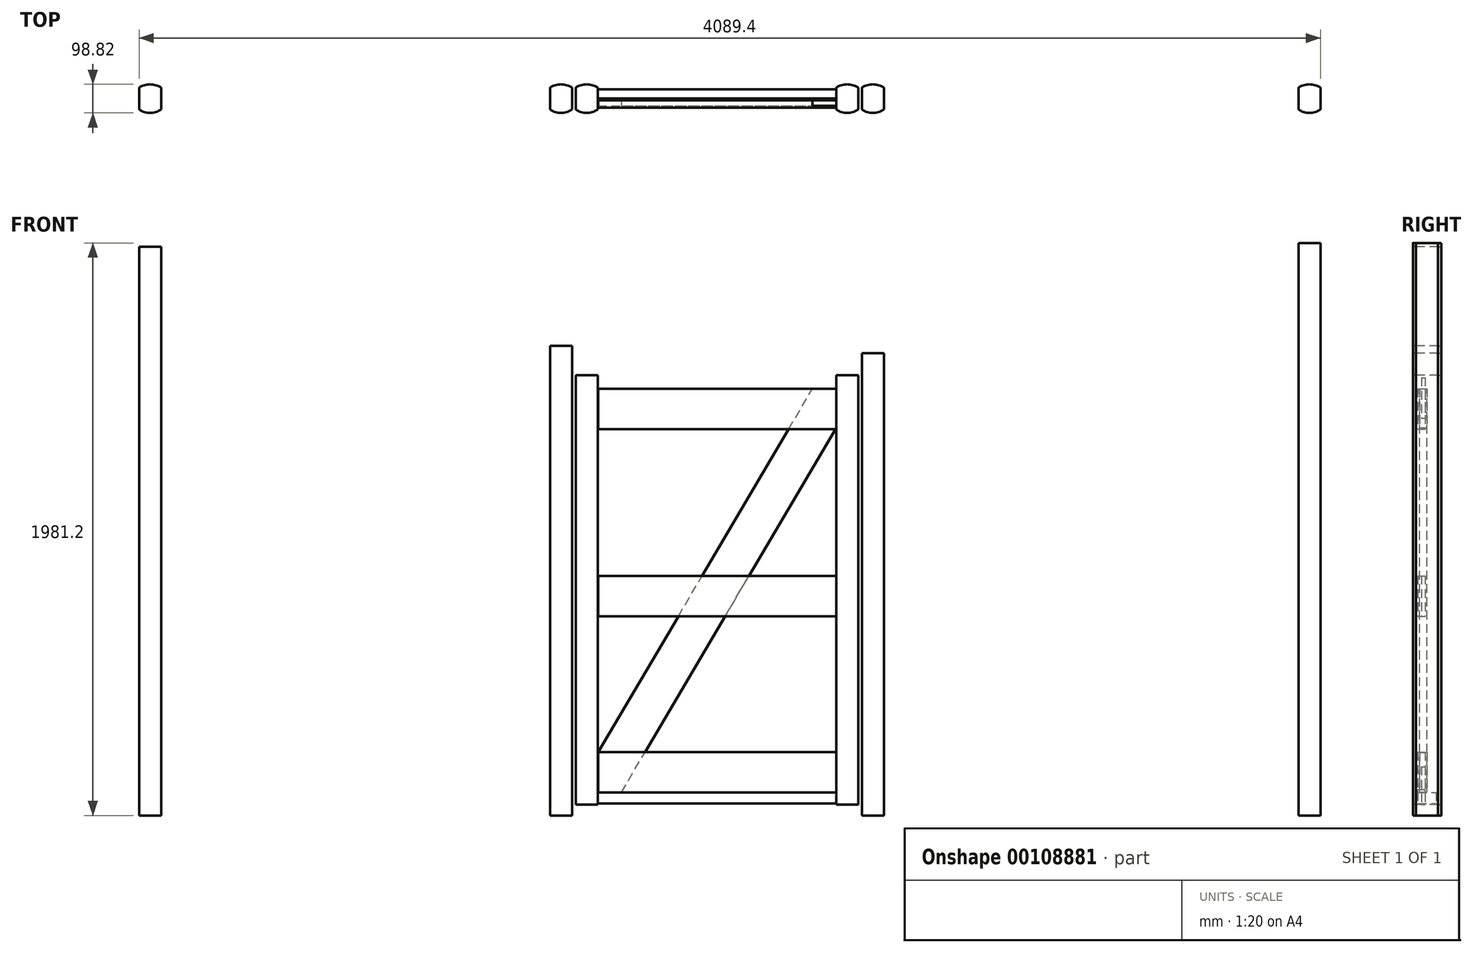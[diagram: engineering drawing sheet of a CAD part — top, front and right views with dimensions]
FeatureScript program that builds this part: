
annotation { "Feature Type Name" : "Feature", "Feature Type Description" : "" }
export const myFeature = defineFeature(function(context is Context, id is Id, definition is map)
    precondition{}
    {
        {
            var Q0;
            Q0=qCreatedBy(makeId("Top.planeOp"),FACE);
            var sketch = newSketch(context, id + "F0", { "sketchPlane" : qUnion([Q0])});
            skLineSegment(sketch, "E0.left", {"start": v(-38.1, 38.1) * mm, "end": v(-38.1, -38.1) * mm});
            skLineSegment(sketch, "E0.right", {"start": v(38.1, 38.1) * mm, "end": v(38.1, -38.1) * mm});
            skPoint(sketch, "E0.middle", {"position": v(0, 0) * mm});
            skArc(sketch, "E1", {"start": v(38.1, 38.1) * mm, "mid": v(0, 49.4) * mm, "end": v(-38.1, 38.1) * mm});
            skArc(sketch, "E2", {"start": v(-38.1, -38.1) * mm, "mid": v(0, -49.4) * mm, "end": v(38.1, -38.1) * mm});
            skSolve(sketch);
        }
        {
            var Q0;
            Q0=makeQuery(id+"F0.imprint","IMPRINT",FACE,{"disambiguationData":[TD([[makeQuery(id+"F0.imprint","IMPRINT",EDGE,{"derivedFrom":sQuery(id+"F0.wireOp",EDGE,"E0.left")}),1.0]])]});
            extrude(context, id + "F1", {"entities" : qUnion([Q0]), "depth" : 1625.6 * mm});
        }
        {
            var Q0;
            Q0=makeQuery(id+"F1.opExtrude","SWEPT_BODY",BODY,{"disambiguationData":[OSD([sQuery(id+"F0.wireOp",EDGE,"E0.left"),sQuery(id+"F0.wireOp",EDGE,"E0.right"),sQuery(id+"F0.wireOp",EDGE,"E1"),sQuery(id+"F0.wireOp",EDGE,"E2")])]});
            transform(context, id + "F2", {"entities" : qUnion([Q0]), "transformType" : TransformType.TRANSLATION_3D, "dx" : 1079.5 * mm, "dy" : 0 * mm, "dz" : 0 * mm, "makeCopy" : true});
        }
        {
            var Q0;
            Q0=makeQuery(id+"F1.opExtrude","SWEPT_BODY",BODY,{"disambiguationData":[OSD([sQuery(id+"F0.wireOp",EDGE,"E0.left"),sQuery(id+"F0.wireOp",EDGE,"E0.right"),sQuery(id+"F0.wireOp",EDGE,"E1"),sQuery(id+"F0.wireOp",EDGE,"E2")])]});
            transform(context, id + "F3", {"entities" : qUnion([Q0]), "transformType" : TransformType.TRANSLATION_3D, "dx" : -1422.4 * mm, "dy" : 0 * mm, "dz" : 0 * mm, "makeCopy" : true});
        }
        {
            var Q0;
            Q0=makeQuery(id+"F3.opPattern","COPY",FACE,{"derivedFrom":makeQuery(id+"F1.opExtrude","CAP_FACE",FACE,{"disambiguationData":[OSD([sQuery(id+"F0.wireOp",EDGE,"E0.left"),sQuery(id+"F0.wireOp",EDGE,"E0.right"),sQuery(id+"F0.wireOp",EDGE,"E1"),sQuery(id+"F0.wireOp",EDGE,"E2")])],"isStart":false}),"instanceName":"1"});
            extrude(context, id + "F4", {"entities" : qUnion([Q0]), "operationType" : NewBodyOperationType.ADD, "depth" : 342.9 * mm});
        }
        {
            var Q0;
            Q0=makeQuery(id+"F2.opPattern","COPY",BODY,{"derivedFrom":makeQuery(id+"F1.opExtrude","SWEPT_BODY",BODY,{"disambiguationData":[OSD([sQuery(id+"F0.wireOp",EDGE,"E0.left"),sQuery(id+"F0.wireOp",EDGE,"E0.right"),sQuery(id+"F0.wireOp",EDGE,"E1"),sQuery(id+"F0.wireOp",EDGE,"E2")])]}),"instanceName":"1"});
            transform(context, id + "F5", {"entities" : qUnion([Q0]), "transformType" : TransformType.TRANSLATION_3D, "dx" : 1511.3 * mm, "dy" : 0 * mm, "dz" : 0 * mm, "makeCopy" : true});
        }
        {
            var Q0;
            Q0=makeQuery(id+"F5.opPattern","COPY",FACE,{"derivedFrom":makeQuery(id+"F2.opPattern","COPY",FACE,{"derivedFrom":makeQuery(id+"F1.opExtrude","CAP_FACE",FACE,{"disambiguationData":[OSD([sQuery(id+"F0.wireOp",EDGE,"E0.left"),sQuery(id+"F0.wireOp",EDGE,"E0.right"),sQuery(id+"F0.wireOp",EDGE,"E1"),sQuery(id+"F0.wireOp",EDGE,"E2")])],"isStart":false}),"instanceName":"1"}),"instanceName":"1"});
            extrude(context, id + "F6", {"entities" : qUnion([Q0]), "operationType" : NewBodyOperationType.ADD, "depth" : 355.6 * mm});
        }
        {
            var Q0;
            Q0=makeQuery(id+"F2.opPattern","COPY",FACE,{"derivedFrom":makeQuery(id+"F1.opExtrude","CAP_FACE",FACE,{"disambiguationData":[OSD([sQuery(id+"F0.wireOp",EDGE,"E0.left"),sQuery(id+"F0.wireOp",EDGE,"E0.right"),sQuery(id+"F0.wireOp",EDGE,"E1"),sQuery(id+"F0.wireOp",EDGE,"E2")])],"isStart":false}),"instanceName":"1"});
            extrude(context, id + "F7", {"entities" : qUnion([Q0]), "operationType" : NewBodyOperationType.REMOVE, "oppositeDirection" : true, "depth" : 25.4 * mm});
        }
        {
            var Q0;
            Q0=makeQuery(id+"F1.opExtrude","SWEPT_BODY",BODY,{"disambiguationData":[OSD([sQuery(id+"F0.wireOp",EDGE,"E0.left"),sQuery(id+"F0.wireOp",EDGE,"E0.right"),sQuery(id+"F0.wireOp",EDGE,"E1"),sQuery(id+"F0.wireOp",EDGE,"E2")])]});
            transform(context, id + "F8", {"entities" : qUnion([Q0]), "transformType" : TransformType.TRANSLATION_3D, "dx" : 88.9 * mm, "dy" : 0 * mm, "dz" : 0 * mm, "makeCopy" : true});
        }
        {
            var Q0;
            Q0=makeQuery(id+"F8.opPattern","COPY",FACE,{"derivedFrom":makeQuery(id+"F1.opExtrude","CAP_FACE",FACE,{"disambiguationData":[OSD([sQuery(id+"F0.wireOp",EDGE,"E0.left"),sQuery(id+"F0.wireOp",EDGE,"E0.right"),sQuery(id+"F0.wireOp",EDGE,"E1"),sQuery(id+"F0.wireOp",EDGE,"E2")])],"isStart":false}),"instanceName":"1"});
            extrude(context, id + "F9", {"entities" : qUnion([Q0]), "operationType" : NewBodyOperationType.REMOVE, "oppositeDirection" : true, "depth" : 76.2 * mm});
        }
        {
            var Q0;
            Q0=makeQuery(id+"F2.opPattern","COPY",BODY,{"derivedFrom":makeQuery(id+"F1.opExtrude","SWEPT_BODY",BODY,{"disambiguationData":[OSD([sQuery(id+"F0.wireOp",EDGE,"E0.left"),sQuery(id+"F0.wireOp",EDGE,"E0.right"),sQuery(id+"F0.wireOp",EDGE,"E1"),sQuery(id+"F0.wireOp",EDGE,"E2")])]}),"instanceName":"1"});
            transform(context, id + "F10", {"entities" : qUnion([Q0]), "transformType" : TransformType.TRANSLATION_3D, "dx" : -88.9 * mm, "dy" : 0 * mm, "dz" : 0 * mm, "makeCopy" : true});
        }
        {
            var Q0;
            Q0=makeQuery(id+"F10.opPattern","COPY",FACE,{"derivedFrom":makeQuery(id+"F7.boolean.opBoolean","COPY",FACE,{"derivedFrom":makeQuery(id+"F7.opExtrude","CAP_FACE",FACE,{"disambiguationData":[OSD([sQuery(id+"F0.wireOp",EDGE,"E0.left"),sQuery(id+"F0.wireOp",EDGE,"E0.right"),sQuery(id+"F0.wireOp",EDGE,"E1"),sQuery(id+"F0.wireOp",EDGE,"E2")])],"isStart":false})}),"instanceName":"1"});
            extrude(context, id + "F11", {"entities" : qUnion([Q0]), "operationType" : NewBodyOperationType.REMOVE, "oppositeDirection" : true, "depth" : 76.2 * mm});
        }
        {
            var Q0;
            Q0=qCreatedBy(makeId("Front.planeOp"),FACE);
            var sketch = newSketch(context, id + "F12", { "sketchPlane" : qUnion([Q0])});
            skLineSegment(sketch, "E3.bottom", {"start": v(128.3, -9.05) * mm, "end": v(953.8, -9.05) * mm});
            skLineSegment(sketch, "E3.top", {"start": v(128.3, -148.75) * mm, "end": v(953.8, -148.75) * mm});
            skLineSegment(sketch, "E3.left", {"start": v(128.3, -9.05) * mm, "end": v(128.3, -148.75) * mm});
            skLineSegment(sketch, "E3.right", {"start": v(953.8, -9.05) * mm, "end": v(953.8, -148.75) * mm});
            skSolve(sketch);
        }
        {
            var Q0;
            Q0 = qSketchRegion(id + "F12", true);
            extrude(context, id + "F13", {"entities" : qUnion([Q0]), "depth" : 38.1 * mm});
        }
        {
            var Q0;
            Q0=makeQuery(id+"F13.opExtrude","SWEPT_BODY",BODY,{"disambiguationData":[OSD([sQuery(id+"F12.wireOp",EDGE,"E3.bottom"),sQuery(id+"F12.wireOp",EDGE,"E3.top"),sQuery(id+"F12.wireOp",EDGE,"E3.left"),sQuery(id+"F12.wireOp",EDGE,"E3.right")])]});
            transform(context, id + "F14", {"entities" : qUnion([Q0]), "transformType" : TransformType.TRANSLATION_3D, "dx" : 0 * mm, "dy" : 0 * mm, "dz" : 1524 * mm, "makeCopy" : true});
        }
        {
            var Q0;
            Q0=makeQuery(id+"F13.opExtrude","SWEPT_BODY",BODY,{"disambiguationData":[OSD([sQuery(id+"F12.wireOp",EDGE,"E3.bottom"),sQuery(id+"F12.wireOp",EDGE,"E3.top"),sQuery(id+"F12.wireOp",EDGE,"E3.left"),sQuery(id+"F12.wireOp",EDGE,"E3.right")])]});
            transform(context, id + "F15", {"entities" : qUnion([Q0]), "transformType" : TransformType.TRANSLATION_3D, "dx" : 0 * mm, "dy" : 0 * mm, "dz" : 177.8 * mm, "makeCopy" : true});
        }
        {
            var Q0;
            Q0=makeQuery(id+"F13.opExtrude","SWEPT_BODY",BODY,{"disambiguationData":[OSD([sQuery(id+"F12.wireOp",EDGE,"E3.bottom"),sQuery(id+"F12.wireOp",EDGE,"E3.top"),sQuery(id+"F12.wireOp",EDGE,"E3.left"),sQuery(id+"F12.wireOp",EDGE,"E3.right")])]});
            transform(context, id + "F16", {"entities" : qUnion([Q0]), "transformType" : TransformType.TRANSLATION_3D, "dx" : 0 * mm, "dy" : 0 * mm, "dz" : 838.2 * mm, "makeCopy" : false});
        }
        {
            var Q0;
            Q0=makeQuery(id+"F14.opPattern","COPY",BODY,{"derivedFrom":makeQuery(id+"F13.opExtrude","SWEPT_BODY",BODY,{"disambiguationData":[OSD([sQuery(id+"F12.wireOp",EDGE,"E3.bottom"),sQuery(id+"F12.wireOp",EDGE,"E3.top"),sQuery(id+"F12.wireOp",EDGE,"E3.left"),sQuery(id+"F12.wireOp",EDGE,"E3.right")])]}),"instanceName":"1"});
            var Q1;
            Q1=makeQuery(id+"F13.opExtrude","SWEPT_BODY",BODY,{"disambiguationData":[OSD([sQuery(id+"F12.wireOp",EDGE,"E3.bottom"),sQuery(id+"F12.wireOp",EDGE,"E3.top"),sQuery(id+"F12.wireOp",EDGE,"E3.left"),sQuery(id+"F12.wireOp",EDGE,"E3.right")])]});
            var Q2;
            Q2=makeQuery(id+"F15.opPattern","COPY",BODY,{"derivedFrom":makeQuery(id+"F13.opExtrude","SWEPT_BODY",BODY,{"disambiguationData":[OSD([sQuery(id+"F12.wireOp",EDGE,"E3.bottom"),sQuery(id+"F12.wireOp",EDGE,"E3.top"),sQuery(id+"F12.wireOp",EDGE,"E3.left"),sQuery(id+"F12.wireOp",EDGE,"E3.right")])]}),"instanceName":"1"});
            transform(context, id + "F17", {"entities" : qUnion([Q0, Q1, Q2]), "transformType" : TransformType.TRANSLATION_3D, "dx" : 0 * mm, "dy" : 19.05 * mm, "dz" : 0 * mm, "makeCopy" : false});
        }
        {
            var Q0;
            Q0=makeQuery(id+"F9.boolean.opBoolean","COPY",FACE,{"derivedFrom":makeQuery(id+"F9.opExtrude","CAP_FACE",FACE,{"disambiguationData":[OSD([sQuery(id+"F0.wireOp",EDGE,"E0.left"),sQuery(id+"F0.wireOp",EDGE,"E0.right"),sQuery(id+"F0.wireOp",EDGE,"E1"),sQuery(id+"F0.wireOp",EDGE,"E2")])],"isStart":false})});
            extrude(context, id + "F18", {"entities" : qUnion([Q0]), "operationType" : NewBodyOperationType.REMOVE, "oppositeDirection" : true, "depth" : 25.4 * mm});
        }
        {
            var Q0;
            Q0=makeQuery(id+"F14.opPattern","COPY",FACE,{"derivedFrom":makeQuery(id+"F13.opExtrude","CAP_FACE",FACE,{"disambiguationData":[OSD([sQuery(id+"F12.wireOp",EDGE,"E3.bottom"),sQuery(id+"F12.wireOp",EDGE,"E3.top"),sQuery(id+"F12.wireOp",EDGE,"E3.left"),sQuery(id+"F12.wireOp",EDGE,"E3.right")])],"isStart":false}),"instanceName":"1"});
            extrude(context, id + "F19", {"entities" : qUnion([Q0]), "operationType" : NewBodyOperationType.REMOVE, "oppositeDirection" : true, "depth" : 12.7 * mm});
        }
        {
            var Q0;
            Q0=makeQuery(id+"F13.opExtrude","CAP_FACE",FACE,{"disambiguationData":[OSD([sQuery(id+"F12.wireOp",EDGE,"E3.bottom"),sQuery(id+"F12.wireOp",EDGE,"E3.top"),sQuery(id+"F12.wireOp",EDGE,"E3.left"),sQuery(id+"F12.wireOp",EDGE,"E3.right")])],"isStart":false});
            extrude(context, id + "F20", {"entities" : qUnion([Q0]), "operationType" : NewBodyOperationType.REMOVE, "oppositeDirection" : true, "depth" : 12.7 * mm});
        }
        {
            var Q0;
            Q0=makeQuery(id+"F15.opPattern","COPY",FACE,{"derivedFrom":makeQuery(id+"F13.opExtrude","CAP_FACE",FACE,{"disambiguationData":[OSD([sQuery(id+"F12.wireOp",EDGE,"E3.bottom"),sQuery(id+"F12.wireOp",EDGE,"E3.top"),sQuery(id+"F12.wireOp",EDGE,"E3.left"),sQuery(id+"F12.wireOp",EDGE,"E3.right")])],"isStart":false}),"instanceName":"1"});
            extrude(context, id + "F21", {"entities" : qUnion([Q0]), "operationType" : NewBodyOperationType.REMOVE, "oppositeDirection" : true, "depth" : 12.7 * mm});
        }
        {
            var Q0;
            Q0=makeQuery(id+"F14.opPattern","COPY",BODY,{"derivedFrom":makeQuery(id+"F13.opExtrude","SWEPT_BODY",BODY,{"disambiguationData":[OSD([sQuery(id+"F12.wireOp",EDGE,"E3.bottom"),sQuery(id+"F12.wireOp",EDGE,"E3.top"),sQuery(id+"F12.wireOp",EDGE,"E3.left"),sQuery(id+"F12.wireOp",EDGE,"E3.right")])]}),"instanceName":"1"});
            var Q1;
            Q1=makeQuery(id+"F13.opExtrude","SWEPT_BODY",BODY,{"disambiguationData":[OSD([sQuery(id+"F12.wireOp",EDGE,"E3.bottom"),sQuery(id+"F12.wireOp",EDGE,"E3.top"),sQuery(id+"F12.wireOp",EDGE,"E3.left"),sQuery(id+"F12.wireOp",EDGE,"E3.right")])]});
            var Q2;
            Q2=makeQuery(id+"F15.opPattern","COPY",BODY,{"derivedFrom":makeQuery(id+"F13.opExtrude","SWEPT_BODY",BODY,{"disambiguationData":[OSD([sQuery(id+"F12.wireOp",EDGE,"E3.bottom"),sQuery(id+"F12.wireOp",EDGE,"E3.top"),sQuery(id+"F12.wireOp",EDGE,"E3.left"),sQuery(id+"F12.wireOp",EDGE,"E3.right")])]}),"instanceName":"1"});
            transform(context, id + "F22", {"entities" : qUnion([Q0, Q1, Q2]), "transformType" : TransformType.TRANSLATION_3D, "dx" : 0 * mm, "dy" : -6.35 * mm, "dz" : 0 * mm, "makeCopy" : false});
        }
        {
            var Q0;
            Q0=makeQuery(id+"F14.opPattern","COPY",BODY,{"derivedFrom":makeQuery(id+"F13.opExtrude","SWEPT_BODY",BODY,{"disambiguationData":[OSD([sQuery(id+"F12.wireOp",EDGE,"E3.bottom"),sQuery(id+"F12.wireOp",EDGE,"E3.top"),sQuery(id+"F12.wireOp",EDGE,"E3.left"),sQuery(id+"F12.wireOp",EDGE,"E3.right")])]}),"instanceName":"1"});
            transform(context, id + "F23", {"entities" : qUnion([Q0]), "transformType" : TransformType.TRANSLATION_3D, "dx" : 0 * mm, "dy" : 0 * mm, "dz" : -38.1 * mm, "makeCopy" : false});
        }
        {
            var Q0;
            Q0=makeQuery(id+"F8.opPattern","COPY",FACE,{"derivedFrom":makeQuery(id+"F1.opExtrude","CAP_FACE",FACE,{"disambiguationData":[OSD([sQuery(id+"F0.wireOp",EDGE,"E0.left"),sQuery(id+"F0.wireOp",EDGE,"E0.right"),sQuery(id+"F0.wireOp",EDGE,"E1"),sQuery(id+"F0.wireOp",EDGE,"E2")])],"isStart":true}),"instanceName":"1"});
            extrude(context, id + "F24", {"entities" : qUnion([Q0]), "operationType" : NewBodyOperationType.REMOVE, "oppositeDirection" : true, "depth" : 38.1 * mm});
        }
        {
            var Q0;
            Q0=makeQuery(id+"F10.opPattern","COPY",FACE,{"derivedFrom":makeQuery(id+"F2.opPattern","COPY",FACE,{"derivedFrom":makeQuery(id+"F1.opExtrude","CAP_FACE",FACE,{"disambiguationData":[OSD([sQuery(id+"F0.wireOp",EDGE,"E0.left"),sQuery(id+"F0.wireOp",EDGE,"E0.right"),sQuery(id+"F0.wireOp",EDGE,"E1"),sQuery(id+"F0.wireOp",EDGE,"E2")])],"isStart":true}),"instanceName":"1"}),"instanceName":"1"});
            extrude(context, id + "F25", {"entities" : qUnion([Q0]), "operationType" : NewBodyOperationType.REMOVE, "oppositeDirection" : true, "depth" : 38.1 * mm});
        }
        {
            var Q0;
            Q0=makeQuery(id+"F15.opPattern","COPY",BODY,{"derivedFrom":makeQuery(id+"F13.opExtrude","SWEPT_BODY",BODY,{"disambiguationData":[OSD([sQuery(id+"F12.wireOp",EDGE,"E3.bottom"),sQuery(id+"F12.wireOp",EDGE,"E3.top"),sQuery(id+"F12.wireOp",EDGE,"E3.left"),sQuery(id+"F12.wireOp",EDGE,"E3.right")])]}),"instanceName":"1"});
            transform(context, id + "F26", {"entities" : qUnion([Q0]), "transformType" : TransformType.TRANSLATION_3D, "dx" : 0 * mm, "dy" : 0 * mm, "dz" : 44.45 * mm, "makeCopy" : false});
        }
        {
            var Q0;
            Q0=qCreatedBy(makeId("Front.planeOp"),FACE);
            var sketch = newSketch(context, id + "F27", { "sketchPlane" : qUnion([Q0])});
            skLineSegment(sketch, "E4.bottom", {"start": v(127, 73.5) * mm, "end": v(952.5, 73.5) * mm});
            skLineSegment(sketch, "E4.top", {"start": v(127, 35.4) * mm, "end": v(952.5, 35.4) * mm});
            skLineSegment(sketch, "E4.left", {"start": v(127, 73.5) * mm, "end": v(127, 35.4) * mm});
            skLineSegment(sketch, "E4.right", {"start": v(952.5, 73.5) * mm, "end": v(952.5, 35.4) * mm});
            skSolve(sketch);
        }
        {
            var Q0;
            Q0=makeQuery(id+"F27.imprint","IMPRINT",FACE,{"disambiguationData":[TD([[makeQuery(id+"F27.imprint","IMPRINT",EDGE,{"derivedFrom":sQuery(id+"F27.wireOp",EDGE,"E4.bottom")}),-1.0]])]});
            extrude(context, id + "F28", {"entities" : qUnion([Q0]), "depth" : 63.5 * mm});
        }
        {
            var Q0;
            Q0=makeQuery(id+"F28.opExtrude","SWEPT_BODY",BODY,{"disambiguationData":[OSD([sQuery(id+"F27.wireOp",EDGE,"E4.bottom"),sQuery(id+"F27.wireOp",EDGE,"E4.top"),sQuery(id+"F27.wireOp",EDGE,"E4.left"),sQuery(id+"F27.wireOp",EDGE,"E4.right")])]});
            transform(context, id + "F29", {"entities" : qUnion([Q0]), "transformType" : TransformType.TRANSLATION_3D, "dx" : 0 * mm, "dy" : 31.75 * mm, "dz" : 0 * mm, "makeCopy" : false});
        }
        {
            var Q0;
            Q0=makeQuery(id+"F15.opPattern","COPY",BODY,{"derivedFrom":makeQuery(id+"F13.opExtrude","SWEPT_BODY",BODY,{"disambiguationData":[OSD([sQuery(id+"F12.wireOp",EDGE,"E3.bottom"),sQuery(id+"F12.wireOp",EDGE,"E3.top"),sQuery(id+"F12.wireOp",EDGE,"E3.left"),sQuery(id+"F12.wireOp",EDGE,"E3.right")])]}),"instanceName":"1"});
            var Q1;
            Q1=makeQuery(id+"F28.opExtrude","SWEPT_BODY",BODY,{"disambiguationData":[OSD([sQuery(id+"F27.wireOp",EDGE,"E4.bottom"),sQuery(id+"F27.wireOp",EDGE,"E4.top"),sQuery(id+"F27.wireOp",EDGE,"E4.left"),sQuery(id+"F27.wireOp",EDGE,"E4.right")])]});
            transform(context, id + "F30", {"entities" : qUnion([Q0, Q1]), "transformType" : TransformType.TRANSLATION_3D, "dx" : 0 * mm, "dy" : 0 * mm, "dz" : 6.35 * mm, "makeCopy" : false});
        }
        {
            var Q0;
            Q0=qCreatedBy(makeId("Front.planeOp"),FACE);
            var sketch = newSketch(context, id + "F31", { "sketchPlane" : qUnion([Q0])});
            skLineSegment(sketch, "E5.bottom", {"start": v(128.25, 217.82) * mm, "end": v(870.62, 1476.85) * mm});
            skLineSegment(sketch, "E5.top", {"start": v(209.59, 80.92) * mm, "end": v(953, 1341.7) * mm});
            skLineSegment(sketch, "E6", {"start": v(128.25, 217.82) * mm, "end": v(128.25, 81.12) * mm});
            skLineSegment(sketch, "E7", {"start": v(128.25, 81.12) * mm, "end": v(209.59, 80.92) * mm});
            skLineSegment(sketch, "E8", {"start": v(870.62, 1476.85) * mm, "end": v(952.5, 1476.85) * mm});
            skLineSegment(sketch, "E9", {"start": v(952.5, 1476.85) * mm, "end": v(953, 1341.7) * mm});
            skSolve(sketch);
        }
        {
            var Q0;
            Q0=makeQuery(id+"F31.imprint","IMPRINT",FACE,{"disambiguationData":[TD([[makeQuery(id+"F31.imprint","IMPRINT",EDGE,{"derivedFrom":sQuery(id+"F31.wireOp",EDGE,"E5.bottom")}),-1.0]])]});
            extrude(context, id + "F32", {"entities" : qUnion([Q0]), "depth" : 25.4 * mm});
        }
        {
            var Q0;
            Q0=makeQuery(id+"F15.opPattern","COPY",BODY,{"derivedFrom":makeQuery(id+"F13.opExtrude","SWEPT_BODY",BODY,{"disambiguationData":[OSD([sQuery(id+"F12.wireOp",EDGE,"E3.bottom"),sQuery(id+"F12.wireOp",EDGE,"E3.top"),sQuery(id+"F12.wireOp",EDGE,"E3.left"),sQuery(id+"F12.wireOp",EDGE,"E3.right")])]}),"instanceName":"1"});
            var Q1;
            Q1=makeQuery(id+"F13.opExtrude","SWEPT_BODY",BODY,{"disambiguationData":[OSD([sQuery(id+"F12.wireOp",EDGE,"E3.bottom"),sQuery(id+"F12.wireOp",EDGE,"E3.top"),sQuery(id+"F12.wireOp",EDGE,"E3.left"),sQuery(id+"F12.wireOp",EDGE,"E3.right")])]});
            var Q2;
            Q2=makeQuery(id+"F14.opPattern","COPY",BODY,{"derivedFrom":makeQuery(id+"F13.opExtrude","SWEPT_BODY",BODY,{"disambiguationData":[OSD([sQuery(id+"F12.wireOp",EDGE,"E3.bottom"),sQuery(id+"F12.wireOp",EDGE,"E3.top"),sQuery(id+"F12.wireOp",EDGE,"E3.left"),sQuery(id+"F12.wireOp",EDGE,"E3.right")])]}),"instanceName":"1"});
            transform(context, id + "F33", {"entities" : qUnion([Q0, Q1, Q2]), "transformType" : TransformType.TRANSLATION_3D, "dx" : 0 * mm, "dy" : -19.05 * mm, "dz" : 0 * mm, "makeCopy" : false});
        }
    });
